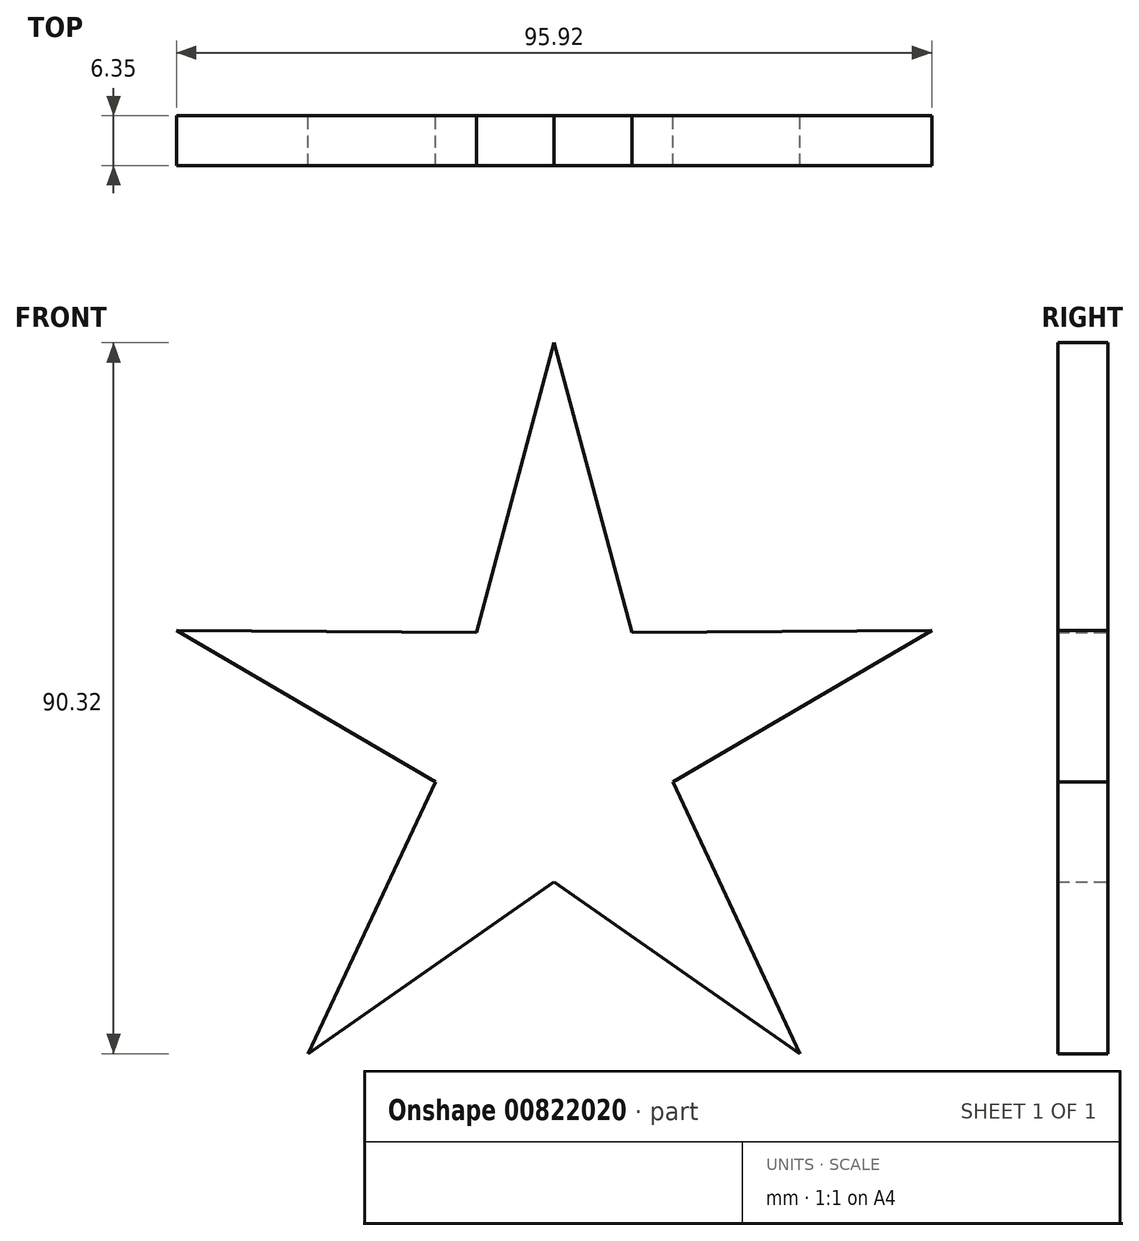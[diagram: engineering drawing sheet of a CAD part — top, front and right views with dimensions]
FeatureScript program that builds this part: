
annotation { "Feature Type Name" : "Feature", "Feature Type Description" : "" }
export const myFeature = defineFeature(function(context is Context, id is Id, definition is map)
    precondition{}
    {
        {
            var Q0;
            Q0=qCreatedBy(makeId("Front.planeOp"),FACE);
            var sketch = newSketch(context, id + "F0", { "sketchPlane" : qUnion([Q0])});
            skLineSegment(sketch, "E0", {"start": v(0, 40) * mm, "end": v(-9.86, 3.2) * mm});
            skLineSegment(sketch, "E1", {"start": v(-9.86, 3.2) * mm, "end": v(-47.96, 3.45) * mm});
            skLineSegment(sketch, "E2", {"start": v(-15.09, -15.81) * mm, "end": v(-47.96, 3.45) * mm});
            skLineSegment(sketch, "E3", {"start": v(-15.09, -15.81) * mm, "end": v(-31.25, -50.31) * mm});
            skLineSegment(sketch, "E4", {"start": v(0, -28.51) * mm, "end": v(-31.25, -50.31) * mm});
            skLineSegment(sketch, "E5", {"start": v(0, 49.56) * mm, "end": v(0, -62.2) * mm});
            skLineSegment(sketch, "E6.MirrorCS", {"start": v(0, 40) * mm, "end": v(9.86, 3.2) * mm});
            skLineSegment(sketch, "E7.MirrorCS", {"start": v(9.86, 3.2) * mm, "end": v(47.96, 3.45) * mm});
            skLineSegment(sketch, "E8.MirrorCS", {"start": v(15.09, -15.81) * mm, "end": v(47.96, 3.45) * mm});
            skLineSegment(sketch, "E9.MirrorCS", {"start": v(15.09, -15.81) * mm, "end": v(31.25, -50.31) * mm});
            skLineSegment(sketch, "E10.MirrorCS", {"start": v(0, -28.51) * mm, "end": v(31.25, -50.31) * mm});
            skSolve(sketch);
        }
        {
            var Q0;
            {var subQ0=sQuery(id+"F0.wireOp",EDGE,"E6.MirrorCS");Q0=makeQuery(id+"F0.imprint","IMPRINT",FACE,{"disambiguationData":[TD([[makeQuery(id+"F0.imprint","IMPRINT",EDGE,{"derivedFrom":subQ0}),-1.0]])]});}
            var Q1;
            {var subQ0=sQuery(id+"F0.wireOp",EDGE,"E0");Q1=makeQuery(id+"F0.imprint","IMPRINT",FACE,{"disambiguationData":[TD([[makeQuery(id+"F0.imprint","IMPRINT",EDGE,{"derivedFrom":subQ0}),1.0]])]});}
            extrude(context, id + "F1", {"entities" : qUnion([Q0, Q1]), "depth" : 6.35 * mm, "offsetDistance" : 25.4 * mm});
        }
    });
